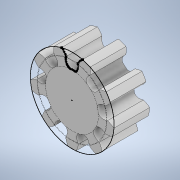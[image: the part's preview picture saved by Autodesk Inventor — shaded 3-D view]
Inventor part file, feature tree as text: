
AUTODESK INVENTOR PART (.ipt)
format: ipt  version: 2022 (Build 260153070, 153G)  size: 219,136 bytes
history: native  units: mm
features: extrude x2, sketch x1, pattern_circular x1
ambient origin geometry x8: Origin, YZ Plane, XZ Plane, XY Plane, X Axis, Y Axis, Z Axis, Center Point
bodies: Solid1 (feature_tree)
feature tree (4):
  sketch  "Sketch1"  dims[d0=3.0mm d1=0.0mm d2=10.0mm d3=0.0mm d4=90.0mm d5=360.0deg]
  extrude  "Extrusion1"  TaperAngle=0.0deg  [1 undecoded]
  extrude  "Extrusion2"  Depth=10.0mm TaperAngle=0.0deg
  pattern_circular  "Circular Pattern1"  Count=9 Angle=360.0deg
note: 1 required parameter value undecoded (feature->parameter linkage not recoverable at this tier; creation-order binding heuristic only, values carry confidence <= 0.55)
